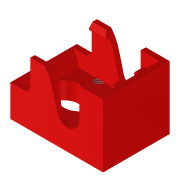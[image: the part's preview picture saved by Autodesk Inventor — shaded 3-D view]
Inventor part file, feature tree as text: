
AUTODESK INVENTOR PART (.ipt)
format: ipt  version: 2021 (Build 250183000, 183)  size: 564,224 bytes
history: native  units: mm
features: sketch x23, extrude x22, projected_geometry x19, fillet x12, chamfer x11, other x3, mirror x2, hole x1, reference x1
ambient origin geometry x8: Origin, YZ Plane, XZ Plane, XY Plane, X Axis, Y Axis, Z Axis, Center Point
bodies: Volumenkörper1 (feature_tree)
feature tree (94):
  extrude  "Extrusion1"  Depth=16.1mm
  extrude  "Extrusion2"  Depth=19.1mm
  extrude  "Extrusion3"  Depth=13.1mm
  extrude  "Extrusion4"  Depth=3.5mm
  extrude  "Extrusion5"  Depth=14.5mm
  chamfer  "Fase1"  [1 undecoded]
  fillet  "Rundung1"  Radius=8.0mm
  mirror  "Spiegeln1"
  extrude  "Extrusion6"  Depth=8.0mm
  mirror  "Spiegeln2"
  extrude  "Extrusion7"  Depth=5.9mm
  chamfer  "Fase2"  Distance=2.0mm
  extrude  "Extrusion8"  Depth=1.5mm
  chamfer  "Fase3"  Distance=2.0mm
  fillet  "Rundung2"  Radius=0.5mm
  fillet  "Rundung3"  Radius=3.65mm
  extrude  "Extrusion9"  Depth=1.5mm
  extrude  "Extrusion10"  Depth=6.0mm
  extrude  "Extrusion11"  Depth=3.0mm TaperAngle=0.0deg
  fillet  "Rundung4"  Radius=12.0mm
  fillet  "Rundung5"  Radius=3.0mm
  extrude  "Extrusion12"  Depth=4.0mm TaperAngle=0.0deg
  hole  "Bohrung1"  [1 undecoded]
  extrude  "Extrusion13"  Depth=0.8mm
  extrude  "Extrusion14"  Depth=3.5mm
  extrude  "Extrusion15"  Depth=2.0mm TaperAngle=0.0deg
  chamfer  "Fase4"  Distance=0.5mm
  fillet  "Rundung6"  Radius=1.0mm
  fillet  "Rundung7"  Radius=1.0mm
  extrude  "Extrusion16"  Depth=3.0mm
  extrude  "Extrusion17"  Depth=1.5mm TaperAngle=0.0deg
  extrude  "Extrusion18"  TaperAngle=0.0deg  [1 undecoded]
  fillet  "Rundung8"  [1 undecoded]
  fillet  "Rundung9"  Radius=10.0mm
  extrude  "Extrusion19"  Depth=5.6mm
  extrude  "Extrusion20"  Depth=1.5mm TaperAngle=0.0deg
  fillet  "Rundung10"  Radius=2.0mm
  extrude  "Extrusion21"  Depth=10.0mm
  chamfer  "Fase5"  Distance=1.0mm
  chamfer  "Fase6"  Distance=14.5mm
  chamfer  "Fase7"  Distance=10.0mm
  chamfer  "Fase8"  Distance=0.05mm
  chamfer  "Fase9"  Distance=5.0mm
  extrude  "Extrusion22"  TaperAngle=0.0deg  [1 undecoded]
  fillet  "Rundung13"  Radius=99.0mm
  chamfer  "Fase10"  Distance=99.0mm
  chamfer  "Fase11"  Distance=1.91mm
  fillet  "Rundung14"  Radius=2.0mm
  sketch  "Skizze1"  dims[d0=23.1mm d1=16.1mm]
  sketch  "Skizze2"  dims[d2=26.1mm d3=19.1mm]
  sketch  "Skizze3"  dims[d4=13.1mm d5=0.0mm d8=5.8mm]
  projected_geometry  "Projizierte Kontur1"
  sketch  "Skizze4"  dims[d9=90.0deg d10=3.5mm]
  projected_geometry  "Projizierte Kontur2"
  sketch  "Skizze5"  dims[d11=2.0mm d12=14.5mm]
  sketch  "Skizze6"  dims[d13=0.0mm]
  sketch  "Skizze7"  dims[d14=4.25mm]
  sketch  "Skizze8"  dims[d15=90.0deg]
  sketch  "Skizze9"  dims[d16=6.5mm d17=0.0mm d18=0.0mm d19=8.0mm]
  sketch  "Skizze10"  dims[d20=0.0mm d21=8.0mm]
  projected_geometry  "Projizierte Kontur3"
  sketch  "Skizze11"  dims[d22=2.5mm d23=5.9mm d24=2.0mm d25=0.0mm]
  projected_geometry  "Projizierte Kontur4"
  sketch  "Skizze12"  dims[d26=0.0mm d27=0.0mm d28=1.5mm d29=2.0mm d30=0.0mm]
  projected_geometry  "Projizierte Kontur5"
  sketch  "Skizze13"  dims[d31=1.2mm d32=2.0mm d33=45.0deg d34=0.5mm d35=3.65mm]
  sketch  "Skizze15"  dims[d36=180.0deg d37=1.5mm]
  reference  "Referenz4"
  projected_geometry  "Projizierte Kontur6"
  sketch  "Skizze16"  dims[d38=2.0mm d39=0.0mm d40=6.0mm]
  projected_geometry  "Projizierte Kontur7"
  sketch  "Skizze17"  dims[d41=3.0mm d42=2.0mm d43=0.0mm]
  projected_geometry  "Projizierte Kontur8"
  sketch  "Skizze18"  dims[d44=1.2mm d45=2.0mm d46=45.0deg d47=12.0mm d48=3.0mm]
  projected_geometry  "Projizierte Kontur9"
  projected_geometry  "Projizierte Kontur10"
  sketch  "Skizze19"  dims[d49=4.0mm d50=2.0mm d51=0.0mm]
  projected_geometry  "Projizierte Kontur11"
  projected_geometry  "Projizierte Kontur12"
  sketch  "Skizze20"  dims[d52=1.2mm d53=2.0mm d54=45.0deg d55=0.5mm]
  projected_geometry  "Projizierte Kontur13"
  sketch  "Skizze21"  dims[d56=0.8mm d57=3.5mm]
  projected_geometry  "Projizierte Kontur14"
  projected_geometry  "Projizierte Kontur15"
  sketch  "Skizze22"  dims[d58=2.0mm d59=3.5mm]
  projected_geometry  "Projizierte Kontur16"
  projected_geometry  "Projizierte Kontur17"
  sketch  "Skizze23"  dims[d60=2.0mm d61=2.0mm d62=0.0mm]
  projected_geometry  "Projizierte Kontur18"
  sketch  "Skizze24"  dims[d63=3.0mm d64=0.5mm d65=0.0mm d66=1.0mm d67=0.0mm d68=1.0mm d69=3.0mm d70=1.5mm d71=0.0mm d72=2.459mm d73=6.0mm d74=6.5mm d75=3.0mm d76=90.0deg d77=6.0mm d78=0.0mm d79=0.0mm d80=0.0mm d81=0.0mm d82=0.0mm d83=10.0mm d84=5.6mm d85=1.5mm d86=0.0mm d87=2.0mm d88=2.0mm d89=11.717774mm d90=10.0mm d91=1.0mm d92=14.5mm d93=10.0mm d94=0.0mm d95=0.05mm d96=0.0mm d97=5.0mm d98=0.0mm d99=0.0mm d100=99.0mm d101=99.0mm d102=1.91mm d103=0.0mm d104=2.0mm d105=0.0mm d106=4.0mm d107=2.0mm d108=0.0mm d109=3.0mm d110=2.0mm d111=4.537856mm d113=0.5mm d114=1.0mm d115=4.537856mm d116=0.5mm d117=1.0mm d118=4.537856mm d119=1.1mm d120=1.0mm d121=4.537856mm d122=1.1mm d123=1.0mm d124=4.537856mm d126=0.1mm d127=0.0mm d128=5.0mm d129=1.0mm d130=2.0mm d131=4.537856mm d132=1.0mm d133=2.0mm d134=4.537856mm d135=10.0mm]
  projected_geometry  "Projizierte Kontur19"
  other  "<userpath>\Desktop\DragonHF\Combined.iam"
  other  "Combined.iam"
  other  "AdxlMount:1"
note: 5 required parameter values undecoded (feature->parameter linkage not recoverable at this tier; creation-order binding heuristic only, values carry confidence <= 0.55)
